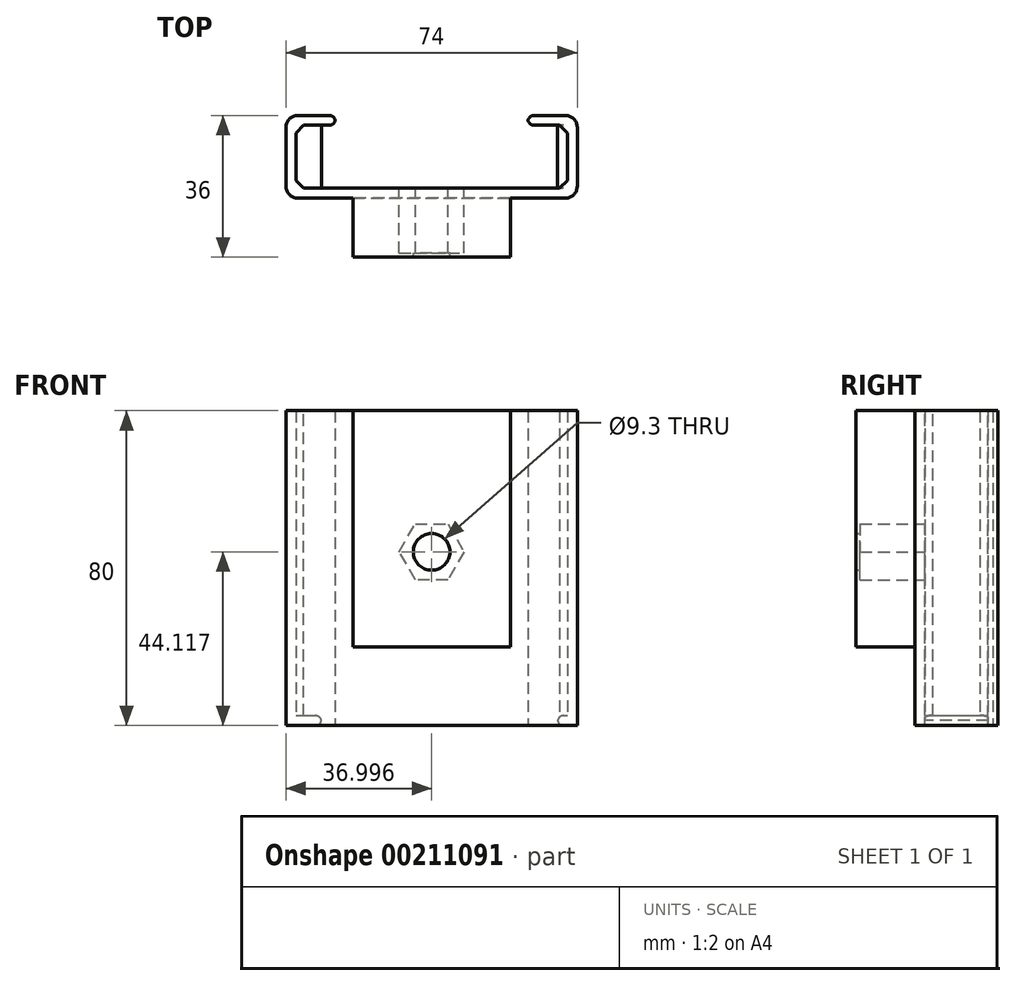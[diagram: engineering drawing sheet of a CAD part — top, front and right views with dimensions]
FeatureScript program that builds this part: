
annotation { "Feature Type Name" : "Feature", "Feature Type Description" : "" }
export const myFeature = defineFeature(function(context is Context, id is Id, definition is map)
    precondition{}
    {
        {
            var Q0;
            Q0=qCreatedBy(makeId("Top.planeOp"),FACE);
            var sketch = newSketch(context, id + "F0", { "sketchPlane" : qUnion([Q0])});
            skLineSegment(sketch, "E0", {"start": v(-24.4, 18.5) * mm, "end": v(-11.9, 18.5) * mm});
            skLineSegment(sketch, "E1", {"start": v(-11.9, 18.5) * mm, "end": v(-11.9, 16) * mm});
            skLineSegment(sketch, "E2", {"start": v(-11.9, 16) * mm, "end": v(-21.9, 16) * mm});
            skLineSegment(sketch, "E3", {"start": v(-21.9, 16) * mm, "end": v(-21.9, 0) * mm});
            skLineSegment(sketch, "E4", {"start": v(-21.9, 0) * mm, "end": v(47.1, 0) * mm});
            skLineSegment(sketch, "E5", {"start": v(47.1, 0) * mm, "end": v(47.1, 16) * mm});
            skLineSegment(sketch, "E6", {"start": v(47.1, 16) * mm, "end": v(37.1, 16) * mm});
            skLineSegment(sketch, "E7", {"start": v(37.1, 16) * mm, "end": v(37.1, 18.5) * mm});
            skLineSegment(sketch, "E8", {"start": v(37.1, 18.5) * mm, "end": v(49.6, 18.5) * mm});
            skLineSegment(sketch, "E9", {"start": v(49.6, 18.5) * mm, "end": v(49.6, -2.5) * mm});
            skLineSegment(sketch, "E10", {"start": v(49.6, -2.5) * mm, "end": v(-24.4, -2.5) * mm});
            skLineSegment(sketch, "E11", {"start": v(-24.4, -2.5) * mm, "end": v(-24.4, 18.5) * mm});
            skLineSegment(sketch, "E12", {"start": v(-15.4, 0) * mm, "end": v(-15.4, 16) * mm});
            skLineSegment(sketch, "E13", {"start": v(44.6, 0) * mm, "end": v(44.6, 16) * mm});
            skSolve(sketch);
        }
        {
            var Q0;
            Q0=makeQuery(id+"F0.imprint","IMPRINT",FACE,{"disambiguationData":[TD([[makeQuery(id+"F0.imprint","IMPRINT",EDGE,{"derivedFrom":sQuery(id+"F0.wireOp",EDGE,"E0")}),-1.0]])]});
            extrude(context, id + "F1", {"entities" : qUnion([Q0]), "depth" : 80 * mm});
        }
        {
            var Q0;
            {var subQ2=sQuery(id+"F0.wireOp",EDGE,"E5");Q0=makeQuery(id+"F0.imprint","IMPRINT",FACE,{"disambiguationData":[TD([[makeQuery(id+"F0.imprint","IMPRINT",EDGE,{"derivedFrom":subQ2}),1.0]])]});}
            var Q1;
            {var subQ2=sQuery(id+"F0.wireOp",EDGE,"E3");Q1=makeQuery(id+"F0.imprint","IMPRINT",FACE,{"disambiguationData":[TD([[makeQuery(id+"F0.imprint","IMPRINT",EDGE,{"derivedFrom":subQ2}),1.0]])]});}
            extrude(context, id + "F2", {"entities" : qUnion([Q0, Q1]), "operationType" : NewBodyOperationType.ADD, "depth" : 2.5 * mm});
        }
        {
            var Q0;
            Q0=makeQuery(id+"F1.opExtrude","SWEPT_EDGE",EDGE,{"disambiguationData":[OSD([sQuery(id+"F0.wireOp",EDGE,"E4"),sQuery(id+"F0.wireOp",EDGE,"E5")])]});
            var Q1;
            Q1=makeQuery(id+"F1.opExtrude","SWEPT_EDGE",EDGE,{"disambiguationData":[OSD([sQuery(id+"F0.wireOp",EDGE,"E5"),sQuery(id+"F0.wireOp",EDGE,"E6")])]});
            var Q2;
            Q2=makeQuery(id+"F1.opExtrude","SWEPT_EDGE",EDGE,{"disambiguationData":[OSD([sQuery(id+"F0.wireOp",EDGE,"E3"),sQuery(id+"F0.wireOp",EDGE,"E4")])]});
            var Q3;
            Q3=makeQuery(id+"F1.opExtrude","SWEPT_EDGE",EDGE,{"disambiguationData":[OSD([sQuery(id+"F0.wireOp",EDGE,"E2"),sQuery(id+"F0.wireOp",EDGE,"E3")])]});
            chamfer(context, id + "F3", {"entities" : qUnion([Q0, Q1, Q2, Q3]), "width" : 2 * mm, "tangentPropagation" : true});
        }
        {
            var Q0;
            Q0=makeQuery(id+"F1.opExtrude","SWEPT_EDGE",EDGE,{"disambiguationData":[OSD([sQuery(id+"F0.wireOp",EDGE,"E0"),sQuery(id+"F0.wireOp",EDGE,"E11")])]});
            var Q1;
            Q1=makeQuery(id+"F1.opExtrude","SWEPT_EDGE",EDGE,{"disambiguationData":[OSD([sQuery(id+"F0.wireOp",EDGE,"E10"),sQuery(id+"F0.wireOp",EDGE,"E11")])]});
            var Q2;
            Q2=makeQuery(id+"F1.opExtrude","SWEPT_EDGE",EDGE,{"disambiguationData":[OSD([sQuery(id+"F0.wireOp",EDGE,"E9"),sQuery(id+"F0.wireOp",EDGE,"E10")])]});
            var Q3;
            Q3=makeQuery(id+"F1.opExtrude","SWEPT_EDGE",EDGE,{"disambiguationData":[OSD([sQuery(id+"F0.wireOp",EDGE,"E8"),sQuery(id+"F0.wireOp",EDGE,"E9")])]});
            fillet(context, id + "F4", {"entities" : qUnion([Q0, Q1, Q2, Q3]), "radius" : 3 * mm, "tangentPropagation" : true, "allowEdgeOverflow" : false});
        }
        {
            var Q0;
            Q0=makeQuery(id+"F1.opExtrude","SWEPT_EDGE",EDGE,{"disambiguationData":[OSD([sQuery(id+"F0.wireOp",EDGE,"E1"),sQuery(id+"F0.wireOp",EDGE,"E2")])]});
            var Q1;
            Q1=makeQuery(id+"F1.opExtrude","SWEPT_EDGE",EDGE,{"disambiguationData":[OSD([sQuery(id+"F0.wireOp",EDGE,"E0"),sQuery(id+"F0.wireOp",EDGE,"E1")])]});
            var Q2;
            Q2=makeQuery(id+"F1.opExtrude","SWEPT_EDGE",EDGE,{"disambiguationData":[OSD([sQuery(id+"F0.wireOp",EDGE,"E7"),sQuery(id+"F0.wireOp",EDGE,"E8")])]});
            var Q3;
            Q3=makeQuery(id+"F1.opExtrude","SWEPT_EDGE",EDGE,{"disambiguationData":[OSD([sQuery(id+"F0.wireOp",EDGE,"E6"),sQuery(id+"F0.wireOp",EDGE,"E7")])]});
            var Q4;
            Q4=makeQuery(id+"F2.opExtrude","CAP_EDGE",EDGE,{"disambiguationData":[OSD([sQuery(id+"F0.wireOp",EDGE,"E13")])],"isStart":false});
            var Q5;
            Q5=makeQuery(id+"F2.opExtrude","CAP_EDGE",EDGE,{"disambiguationData":[OSD([sQuery(id+"F0.wireOp",EDGE,"E13")])],"isStart":true});
            var Q6;
            Q6=makeQuery(id+"F2.opExtrude","CAP_EDGE",EDGE,{"disambiguationData":[OSD([sQuery(id+"F0.wireOp",EDGE,"E12")])],"isStart":false});
            var Q7;
            Q7=makeQuery(id+"F2.opExtrude","CAP_EDGE",EDGE,{"disambiguationData":[OSD([sQuery(id+"F0.wireOp",EDGE,"E12")])],"isStart":true});
            fillet(context, id + "F5", {"entities" : qUnion([Q0, Q1, Q2, Q3, Q4, Q5, Q6, Q7]), "radius" : 1.5 * mm, "tangentPropagation" : true, "allowEdgeOverflow" : false});
        }
        {
            var Q0;
            Q0=makeQuery(id+"F1.opExtrude","SWEPT_FACE",FACE,{"disambiguationData":[OSD([sQuery(id+"F0.wireOp",EDGE,"E10")])]});
            var sketch = newSketch(context, id + "F6", { "sketchPlane" : qUnion([Q0])});
            skCircle(sketch, "E14.cCircle", {"center": v(12.6, 44.12) * mm, "radius": 7.12 * mm, "construction": true});
            skLineSegment(sketch, "E14.0", {"start": v(16.7, 51.24) * mm, "end": v(20.82, 44.12) * mm});
            skLineSegment(sketch, "E14.1", {"start": v(20.82, 44.12) * mm, "end": v(16.7, 37) * mm});
            skLineSegment(sketch, "E14.2", {"start": v(16.7, 37) * mm, "end": v(8.48, 37) * mm});
            skLineSegment(sketch, "E14.3", {"start": v(8.48, 37) * mm, "end": v(4.37, 44.12) * mm});
            skLineSegment(sketch, "E14.4", {"start": v(4.37, 44.12) * mm, "end": v(8.48, 51.24) * mm});
            skLineSegment(sketch, "E14.5", {"start": v(8.48, 51.24) * mm, "end": v(16.7, 51.24) * mm});
            skPoint(sketch, "E14.0.midPoint", {"position": v(18.77, 47.68) * mm});
            skCircle(sketch, "E15", {"center": v(12.6, 44.12) * mm, "radius": 4.65 * mm});
            skPoint(sketch, "E16", {"position": v(12.6, 0) * mm});
            skLineSegment(sketch, "E17", {"start": v(12.6, 0) * mm, "end": v(12.6, 80) * mm, "construction": true});
            skSolve(sketch);
        }
        {
            var Q0;
            Q0=makeQuery(id+"F1.opExtrude","SWEPT_FACE",FACE,{"disambiguationData":[OSD([sQuery(id+"F0.wireOp",EDGE,"E10")])]});
            var sketch = newSketch(context, id + "F7", { "sketchPlane" : qUnion([Q0])});
            skLineSegment(sketch, "E18.bottom", {"start": v(-7.4, 80) * mm, "end": v(32.6, 80) * mm});
            skLineSegment(sketch, "E18.top", {"start": v(-7.4, 20) * mm, "end": v(32.6, 20) * mm});
            skLineSegment(sketch, "E18.left", {"start": v(-7.4, 80) * mm, "end": v(-7.4, 20) * mm});
            skLineSegment(sketch, "E18.right", {"start": v(32.6, 80) * mm, "end": v(32.6, 20) * mm});
            skSolve(sketch);
        }
        {
            var Q0;
            Q0=makeQuery(id+"F7.imprint","IMPRINT",FACE,{"disambiguationData":[TD([[makeQuery(id+"F7.imprint","IMPRINT",EDGE,{"derivedFrom":sQuery(id+"F7.wireOp",EDGE,"E18.bottom")}),1.0]])]});
            extrude(context, id + "F8", {"entities" : qUnion([Q0]), "operationType" : NewBodyOperationType.ADD, "depth" : 15 * mm});
        }
        {
            var Q0;
            Q0 = qSketchRegion(id + "F6", true);
            extrude(context, id + "F9", {"entities" : qUnion([Q0]), "operationType" : NewBodyOperationType.REMOVE, "depth" : 14 * mm, "hasSecondDirection" : true, "secondDirectionOppositeDirection" : true, "secondDirectionDepth" : 25 * mm});
        }
        {
            var Q0;
            Q0=makeQuery(id+"F9.boolean.opBoolean","SPLIT",FACE,{"disambiguationData":[TD([makeQuery(id+"F9.opExtrude","SWEPT_FACE",FACE,{"disambiguationData":[OSD([sQuery(id+"F6.wireOp",EDGE,"E15")])]})])],"derivedFrom":makeQuery(id+"F1.opExtrude","SWEPT_FACE",FACE,{"disambiguationData":[OSD([sQuery(id+"F0.wireOp",EDGE,"E4")])]})});
            var sketch = newSketch(context, id + "F10", { "sketchPlane" : qUnion([Q0])});
            skSolve(sketch);
        }
        {
            var Q0;
            Q0 = qSketchRegion(id + "F10", true);
            var Q1;
            Q1=makeQuery(id+"F10.imprint","IMPRINT",FACE,{"disambiguationData":[TD([[makeQuery(id+"F10.imprint","IMPRINT",EDGE,{"derivedFrom":makeQuery(id+"F9.boolean.opBoolean","INTERSECT",EDGE,{"derivedFrom":[makeQuery(id+"F1.opExtrude","SWEPT_FACE",FACE,{"disambiguationData":[OSD([sQuery(id+"F0.wireOp",EDGE,"E4")])]}),makeQuery(id+"F9.opExtrude","SWEPT_FACE",FACE,{"disambiguationData":[OSD([sQuery(id+"F6.wireOp",EDGE,"E15")])]})]})}),-1.0]])]});
            extrude(context, id + "F11", {"entities" : qUnion([Q0, Q1]), "operationType" : NewBodyOperationType.REMOVE, "oppositeDirection" : true, "depth" : 25 * mm});
        }
    });
